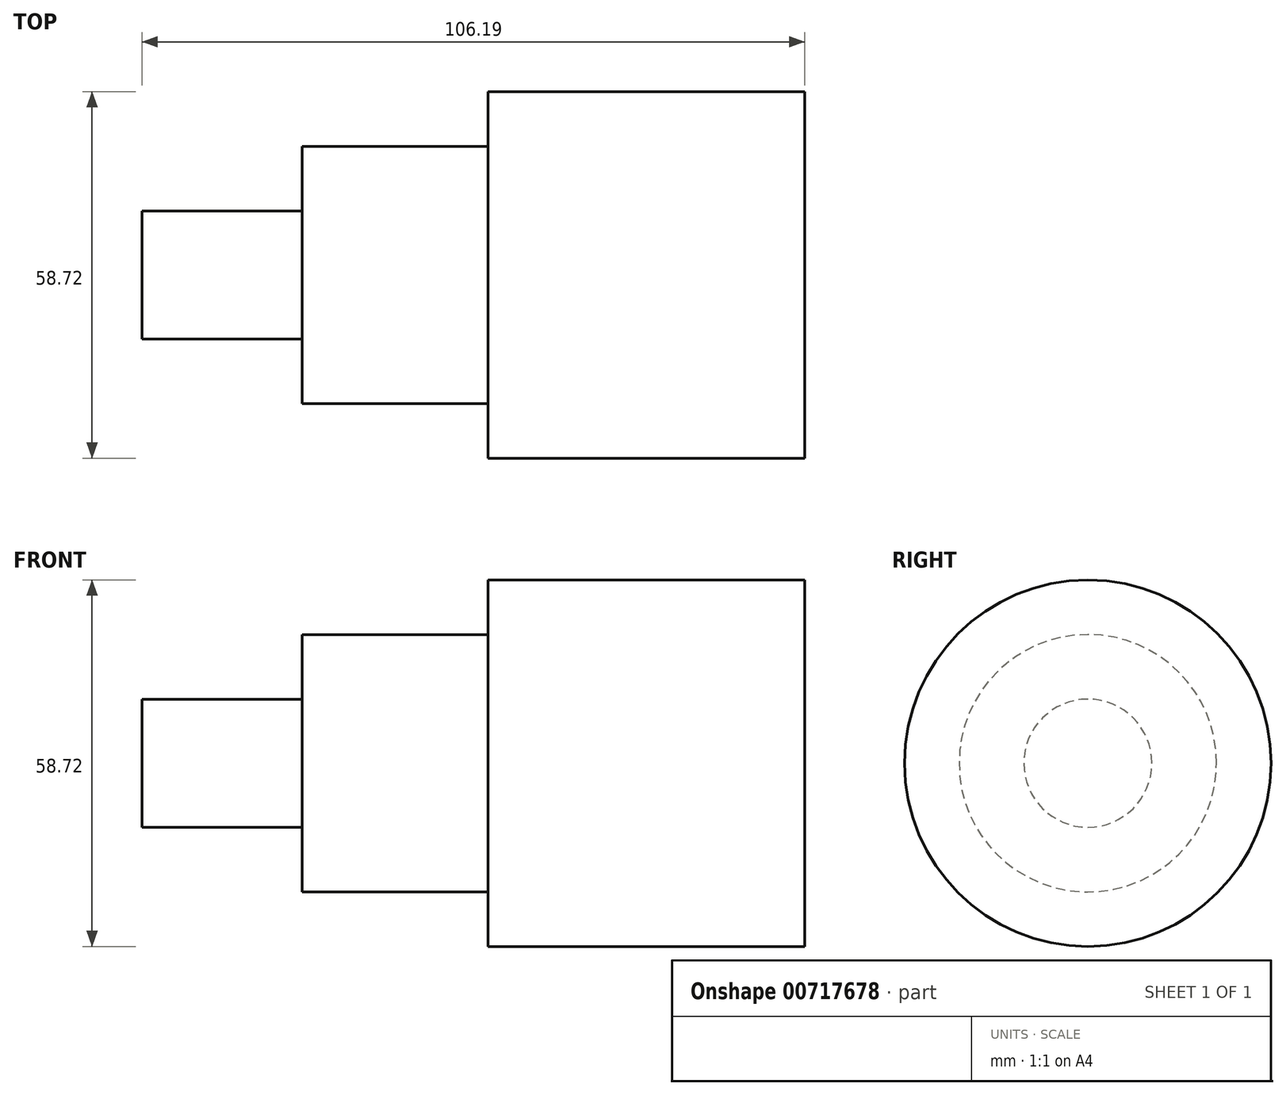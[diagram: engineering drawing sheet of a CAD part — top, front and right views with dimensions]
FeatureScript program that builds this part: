
annotation { "Feature Type Name" : "Feature", "Feature Type Description" : "" }
export const myFeature = defineFeature(function(context is Context, id is Id, definition is map)
    precondition{}
    {
        {
            var Q0;
            Q0=qCreatedBy(makeId("Front.planeOp"),FACE);
            var sketch = newSketch(context, id + "F0", { "sketchPlane" : qUnion([Q0])});
            skLineSegment(sketch, "E0", {"start": v(0, 0) * mm, "end": v(-106.19, 0) * mm});
            skLineSegment(sketch, "E1", {"start": v(-106.19, 0) * mm, "end": v(-106.19, 10.26) * mm});
            skLineSegment(sketch, "E2", {"start": v(-106.19, 10.26) * mm, "end": v(-80.54, 10.26) * mm});
            skLineSegment(sketch, "E3", {"start": v(-80.54, 10.26) * mm, "end": v(-80.54, 20.62) * mm});
            skLineSegment(sketch, "E4", {"start": v(-80.54, 20.62) * mm, "end": v(-50.74, 20.62) * mm});
            skLineSegment(sketch, "E5", {"start": v(-50.74, 20.62) * mm, "end": v(-50.74, 29.36) * mm});
            skLineSegment(sketch, "E6", {"start": v(-50.74, 29.36) * mm, "end": v(0, 29.36) * mm});
            skLineSegment(sketch, "E7", {"start": v(0, 29.36) * mm, "end": v(0, 0) * mm});
            skSolve(sketch);
        }
        {
            var Q0;
            Q0=makeQuery(id+"F0.imprint","IMPRINT",FACE,{"disambiguationData":[TD([[makeQuery(id+"F0.imprint","IMPRINT",EDGE,{"derivedFrom":sQuery(id+"F0.wireOp",EDGE,"E0")}),-1.0]])]});
            var Q1;
            Q1=sQuery(id+"F0.wireOp",EDGE,"E0");
            revolve(context, id + "F1", {"surfaceOperationType" : NewSurfaceOperationType.NEW, "entities" : qUnion([Q0]), "axis" : qUnion([Q1]), "revolveType" : RevolveType.FULL});
        }
    });
